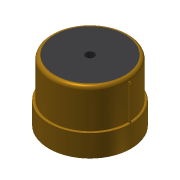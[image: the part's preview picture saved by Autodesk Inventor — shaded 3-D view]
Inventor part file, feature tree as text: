
AUTODESK INVENTOR PART (.ipt)
format: ipt  version: 2014 SP1 (Build 180222100, 222)  size: 154,112 bytes
history: native  units: in
note: dims shown in document units (in); Inventor stores cm internally (conversion verified against a paired STEP export)
features: extrude x5, sketch x5, chamfer x2, fillet x2
ambient origin geometry x8: Origin, YZ Plane, XZ Plane, XY Plane, X Axis, Y Axis, Z Axis, Center Point
bodies: Solid1 (feature_tree)
feature tree (14):
  extrude  "Extrusion1"  Depth=0.312in TaperAngle=0.0deg
  extrude  "Extrusion2"  Depth=0.55in TaperAngle=0.0deg
  extrude  "Extrusion3"  TaperAngle=180.0deg  [1 undecoded]
  chamfer  "Chamfer1"  Distance=0.5in
  chamfer  "Chamfer2"  Distance=0.02in Angle=45.0deg
  fillet  "Fillet1"  Radius=0.05in
  fillet  "Fillet2"  Radius=0.02in
  extrude  "Extrusion4"  Depth=1.0in TaperAngle=0.0deg
  extrude  "Extrusion5"  Depth=0.1181in
  sketch  "Sketch1"  dims[d0=1.16in d1=0.312in d2=0.0in]
  sketch  "Sketch2"  dims[d3=1.095in d4=0.55in d5=0.0in]
  sketch  "Sketch4"  dims[d7=180.0deg d8=180.0deg d9=0.5in d10=0.0in d11=0.02in d12=0.125in d13=45.0deg]
  sketch  "Sketch5"  dims[d14=0.02in d15=0.125in d16=45.0deg d17=0.05in d18=0.02in]
  sketch  "Sketch6"  dims[d19=0.625in d20=1.0in d21=0.0in d22=0.1181in d23=0.862in d24=0.0in]
note: 1 required parameter value undecoded (feature->parameter linkage not recoverable at this tier; creation-order binding heuristic only, values carry confidence <= 0.55)
